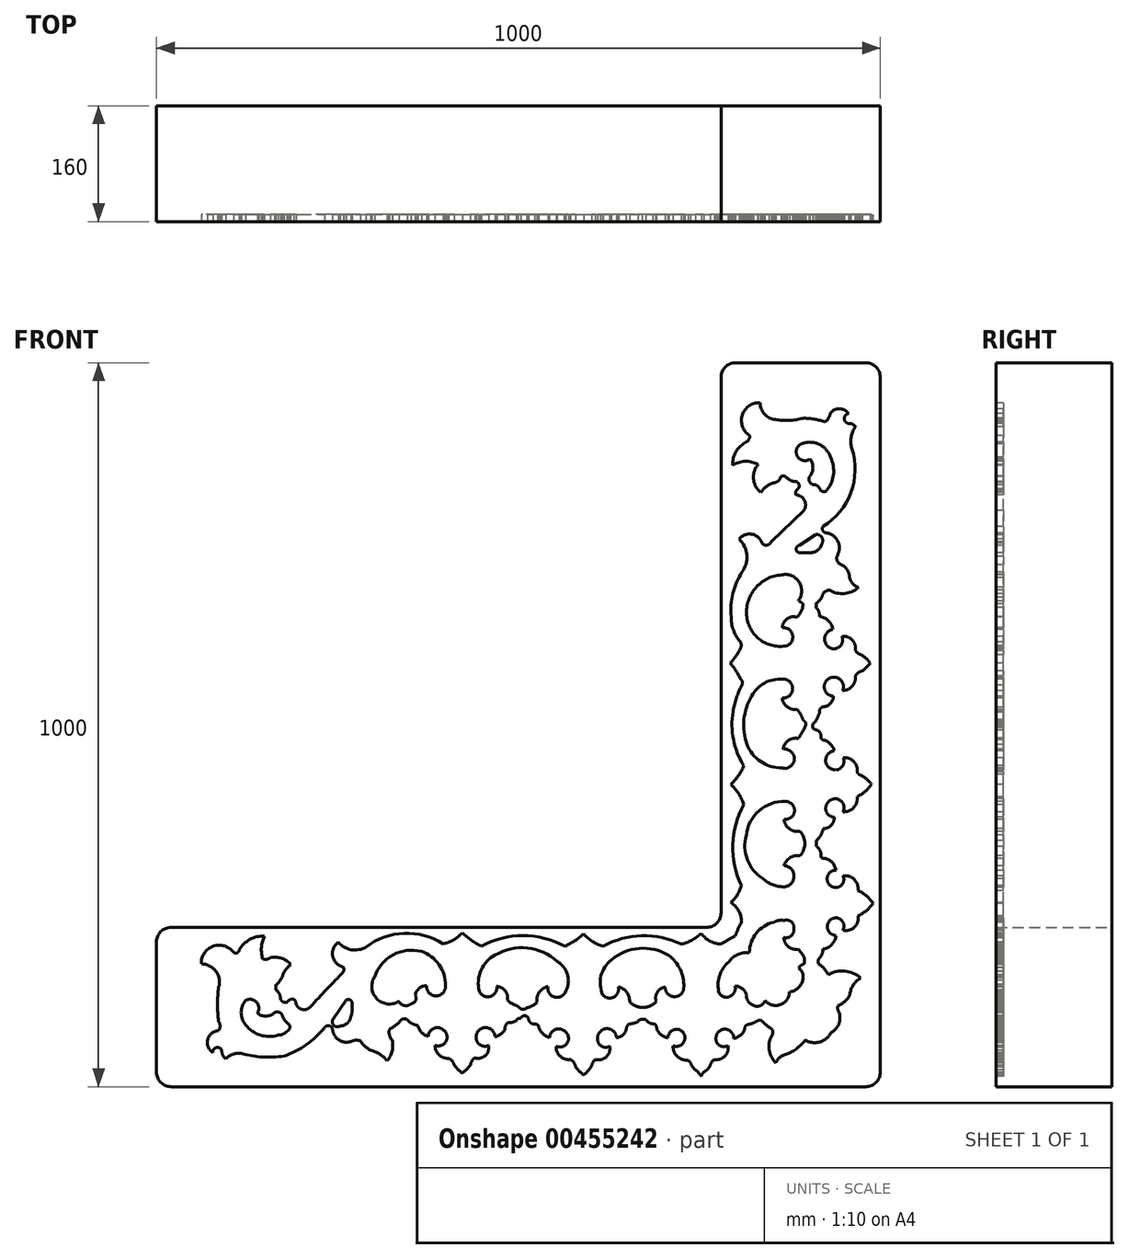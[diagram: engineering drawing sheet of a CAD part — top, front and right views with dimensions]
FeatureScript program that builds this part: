
annotation { "Feature Type Name" : "Feature", "Feature Type Description" : "" }
export const myFeature = defineFeature(function(context is Context, id is Id, definition is map)
    precondition{}
    {
        {
            var Q0;
            Q0=qCreatedBy(makeId("Front.planeOp"),FACE);
            var sketch = newSketch(context, id + "F0", { "sketchPlane" : qUnion([Q0])});
            skLineSegment(sketch, "E0", {"start": v(293.54, 525.11) * mm, "end": v(513.54, 525.11) * mm});
            skLineSegment(sketch, "E1", {"start": v(513.54, 525.11) * mm, "end": v(513.54, -474.89) * mm});
            skLineSegment(sketch, "E2", {"start": v(513.54, -474.89) * mm, "end": v(-486.46, -474.89) * mm});
            skLineSegment(sketch, "E3", {"start": v(-486.46, -474.89) * mm, "end": v(-486.46, -254.89) * mm});
            skLineSegment(sketch, "E4", {"start": v(-486.46, -254.89) * mm, "end": v(293.54, -254.89) * mm});
            skLineSegment(sketch, "E5", {"start": v(293.54, -254.89) * mm, "end": v(293.54, 525.11) * mm});
            skSolve(sketch);
        }
        {
            var Q0;
            Q0=makeQuery(id+"F0.imprint","IMPRINT",FACE,{"disambiguationData":[TD([[makeQuery(id+"F0.imprint","IMPRINT",EDGE,{"derivedFrom":sQuery(id+"F0.wireOp",EDGE,"E0")}),-1.0]])]});
            extrude(context, id + "F1", {"entities" : qUnion([Q0]), "depth" : 160 * mm, "offsetDistance" : 25 * mm});
        }
        {
            var Q0;
            Q0=makeQuery(id+"F1.opExtrude","CAP_FACE",FACE,{"disambiguationData":[OSD([sQuery(id+"F0.wireOp",EDGE,"E0"),sQuery(id+"F0.wireOp",EDGE,"E1"),sQuery(id+"F0.wireOp",EDGE,"E2"),sQuery(id+"F0.wireOp",EDGE,"E3"),sQuery(id+"F0.wireOp",EDGE,"E4"),sQuery(id+"F0.wireOp",EDGE,"E5")])],"isStart":false});
            var sketch = newSketch(context, id + "F2", { "sketchPlane" : qUnion([Q0])});
            skLineSegment(sketch, "E6.0", {"start": v(-486.46, -474.89) * mm, "end": v(-486.46, -254.89) * mm});
            skLineSegment(sketch, "E7.0", {"start": v(-486.46, -254.89) * mm, "end": v(293.54, -254.89) * mm});
            skLineSegment(sketch, "E8.0", {"start": v(293.54, -254.89) * mm, "end": v(293.54, 525.11) * mm});
            skLineSegment(sketch, "E9.0", {"start": v(513.54, 525.11) * mm, "end": v(513.54, -474.89) * mm});
            skLineSegment(sketch, "E10.0", {"start": v(293.54, 525.11) * mm, "end": v(513.54, 525.11) * mm});
            skLineSegment(sketch, "E11.0", {"start": v(513.54, -474.89) * mm, "end": v(-486.46, -474.89) * mm});
            skPoint(sketch, "E12", {"position": v(347.58, 469.9) * mm});
            skPoint(sketch, "E13", {"position": v(469.47, 454.84) * mm});
            skPoint(sketch, "E14", {"position": v(479.4, 436.57) * mm});
            skPoint(sketch, "E15", {"position": v(416.47, 392.08) * mm});
            skPoint(sketch, "E16", {"position": v(309.46, 383.32) * mm});
            skPoint(sketch, "E17", {"position": v(348.57, 346) * mm});
            skPoint(sketch, "E18", {"position": v(397.01, 342.64) * mm});
            skArc(sketch, "E19", {"start": v(347.58, 469.9) * mm, "mid": v(322.83, 452.99) * mm, "end": v(333.09, 424.82) * mm});
            skArc(sketch, "E20", {"start": v(347.58, 469.9) * mm, "mid": v(353.59, 454.2) * mm, "end": v(368.62, 446.67) * mm});
            skArc(sketch, "E21", {"start": v(368.62, 446.67) * mm, "mid": v(387.58, 445.56) * mm, "end": v(406.34, 448.47) * mm});
            skArc(sketch, "E22", {"start": v(436.71, 443.51) * mm, "mid": v(421.76, 447.44) * mm, "end": v(406.34, 448.47) * mm});
            skArc(sketch, "E23", {"start": v(436.71, 443.51) * mm, "mid": v(441.95, 448.43) * mm, "end": v(444.26, 455.23) * mm});
            skArc(sketch, "E24", {"start": v(469.47, 454.84) * mm, "mid": v(456.97, 461.6) * mm, "end": v(444.26, 455.23) * mm});
            skArc(sketch, "E25", {"start": v(469.47, 454.84) * mm, "mid": v(463.74, 448.09) * mm, "end": v(469.47, 441.34) * mm});
            skArc(sketch, "E26", {"start": v(479.4, 436.57) * mm, "mid": v(475.12, 440.38) * mm, "end": v(469.47, 441.34) * mm});
            skArc(sketch, "E27", {"start": v(328.32, 415.69) * mm, "mid": v(332.21, 419.47) * mm, "end": v(333.09, 424.82) * mm});
            skArc(sketch, "E28", {"start": v(328.32, 415.69) * mm, "mid": v(314.23, 402.22) * mm, "end": v(309.46, 383.32) * mm});
            skArc(sketch, "E29", {"start": v(344.66, 384.5) * mm, "mid": v(326.9, 389.02) * mm, "end": v(309.46, 383.32) * mm});
            skArc(sketch, "E30", {"start": v(344.66, 384.5) * mm, "mid": v(338.42, 364.41) * mm, "end": v(348.57, 346) * mm});
            skArc(sketch, "E31", {"start": v(368.62, 359.7) * mm, "mid": v(357.18, 354.93) * mm, "end": v(348.57, 346) * mm});
            skArc(sketch, "E32", {"start": v(368.62, 359.7) * mm, "mid": v(373.45, 362.8) * mm, "end": v(376.17, 367.85) * mm});
            skArc(sketch, "E33", {"start": v(382.92, 367.85) * mm, "mid": v(379.54, 368.86) * mm, "end": v(376.17, 367.85) * mm});
            skArc(sketch, "E34", {"start": v(405.15, 413.52) * mm, "mid": v(398.78, 396.46) * mm, "end": v(416.47, 392.08) * mm});
            skArc(sketch, "E35", {"start": v(444.65, 394.87) * mm, "mid": v(428.84, 412.53) * mm, "end": v(405.15, 413.52) * mm});
            skArc(sketch, "E36", {"start": v(416.47, 368.86) * mm, "mid": v(420.54, 380.47) * mm, "end": v(416.47, 392.08) * mm});
            skPoint(sketch, "E36.startSnap0", {"position": v(379.54, 368.86) * mm});
            skArc(sketch, "E37", {"start": v(416.47, 368.86) * mm, "mid": v(416.06, 360.33) * mm, "end": v(423.81, 356.74) * mm});
            skArc(sketch, "E38", {"start": v(431.55, 348.6) * mm, "mid": v(428.43, 353.38) * mm, "end": v(423.81, 356.74) * mm});
            skArc(sketch, "E39", {"start": v(438.7, 347.61) * mm, "mid": v(448.83, 370.34) * mm, "end": v(444.65, 394.87) * mm});
            skArc(sketch, "E40", {"start": v(431.55, 348.6) * mm, "mid": v(435, 347.14) * mm, "end": v(438.7, 347.61) * mm});
            skArc(sketch, "E41", {"start": v(382.92, 367.85) * mm, "mid": v(389.55, 362.82) * mm, "end": v(397.65, 360.91) * mm});
            skArc(sketch, "E42", {"start": v(479.4, 436.57) * mm, "mid": v(473.26, 422.25) * mm, "end": v(474.29, 406.7) * mm});
            skArc(sketch, "E43", {"start": v(434.42, 298.87) * mm, "mid": v(472.97, 345.9) * mm, "end": v(474.29, 406.7) * mm});
            skArc(sketch, "E44", {"start": v(434.42, 298.87) * mm, "mid": v(434.35, 293) * mm, "end": v(439.48, 290.16) * mm});
            skArc(sketch, "E45", {"start": v(400.17, 351.09) * mm, "mid": v(401.39, 356.64) * mm, "end": v(397.65, 360.91) * mm});
            skArc(sketch, "E46", {"start": v(400.17, 351.09) * mm, "mid": v(396.92, 347.49) * mm, "end": v(397.01, 342.64) * mm});
            skArc(sketch, "E47", {"start": v(408.31, 321.32) * mm, "mid": v(408.75, 335.21) * mm, "end": v(397.01, 342.64) * mm});
            skLineSegment(sketch, "E48", {"start": v(408.31, 321.32) * mm, "end": v(362.74, 277.98) * mm});
            skArc(sketch, "E49", {"start": v(350, 276.2) * mm, "mid": v(356.91, 273.14) * mm, "end": v(362.74, 277.98) * mm});
            skArc(sketch, "E50", {"start": v(350, 276.2) * mm, "mid": v(335.85, 288.38) * mm, "end": v(318.5, 281.52) * mm});
            skArc(sketch, "E51", {"start": v(433.32, 276.2) * mm, "mid": v(432.24, 284.82) * mm, "end": v(424.05, 287.72) * mm});
            skArc(sketch, "E52", {"start": v(415.91, 262.73) * mm, "mid": v(427.12, 266.23) * mm, "end": v(433.32, 276.2) * mm});
            skLineSegment(sketch, "E53", {"start": v(424.05, 287.72) * mm, "end": v(401.6, 272.84) * mm});
            skLineSegment(sketch, "E54", {"start": v(415.91, 262.73) * mm, "end": v(402.44, 262.73) * mm});
            skArc(sketch, "E55", {"start": v(401.6, 272.84) * mm, "mid": v(397.36, 267.4) * mm, "end": v(402.44, 262.73) * mm});
            skArc(sketch, "E56", {"start": v(453.53, 257.97) * mm, "mid": v(455.25, 277.88) * mm, "end": v(439.48, 290.16) * mm});
            skArc(sketch, "E57", {"start": v(453.53, 257.97) * mm, "mid": v(454.5, 250.96) * mm, "end": v(459.7, 246.17) * mm});
            skArc(sketch, "E58", {"start": v(322.42, 235.75) * mm, "mid": v(329.22, 259.39) * mm, "end": v(318.5, 281.52) * mm});
            skArc(sketch, "E59", {"start": v(322.42, 235.75) * mm, "mid": v(309.83, 206.4) * mm, "end": v(307.54, 174.54) * mm});
            skArc(sketch, "E60", {"start": v(471.16, 228.58) * mm, "mid": v(467.9, 238.98) * mm, "end": v(459.7, 246.17) * mm});
            skArc(sketch, "E61", {"start": v(471.16, 228.58) * mm, "mid": v(475.53, 220.14) * mm, "end": v(483.44, 214.88) * mm});
            skArc(sketch, "E62", {"start": v(443.28, 211.3) * mm, "mid": v(463.96, 206.3) * mm, "end": v(483.44, 214.88) * mm});
            skArc(sketch, "E63", {"start": v(443.28, 211.3) * mm, "mid": v(436.25, 208.03) * mm, "end": v(432.89, 201.05) * mm});
            skArc(sketch, "E64", {"start": v(424.75, 192.2) * mm, "mid": v(429.03, 196.42) * mm, "end": v(432.89, 201.05) * mm});
            skArc(sketch, "E65", {"start": v(398.3, 173.7) * mm, "mid": v(384.6, 171.37) * mm, "end": v(378.1, 159.1) * mm});
            skArc(sketch, "E66", {"start": v(398.3, 173.7) * mm, "mid": v(404.56, 181.95) * mm, "end": v(406.87, 192.04) * mm});
            skArc(sketch, "E67", {"start": v(406.87, 192.04) * mm, "mid": v(403.8, 194.52) * mm, "end": v(400.27, 196.25) * mm});
            skArc(sketch, "E68", {"start": v(400.27, 196.25) * mm, "mid": v(401.46, 222.16) * mm, "end": v(377.52, 232.15) * mm});
            skArc(sketch, "E69", {"start": v(377.52, 232.15) * mm, "mid": v(340.66, 213.44) * mm, "end": v(329.28, 173.7) * mm});
            skArc(sketch, "E70", {"start": v(329.28, 173.7) * mm, "mid": v(348.5, 141.77) * mm, "end": v(385.06, 134.46) * mm});
            skArc(sketch, "E71", {"start": v(385.06, 134.46) * mm, "mid": v(392.23, 149.8) * mm, "end": v(378.1, 159.1) * mm});
            skArc(sketch, "E72", {"start": v(424.75, 187.29) * mm, "mid": v(425, 189.74) * mm, "end": v(424.75, 192.2) * mm});
            skArc(sketch, "E73", {"start": v(429.85, 174.76) * mm, "mid": v(428.5, 181.51) * mm, "end": v(424.75, 187.29) * mm});
            skArc(sketch, "E74", {"start": v(447.96, 156.74) * mm, "mid": v(441.92, 168.78) * mm, "end": v(429.85, 174.76) * mm});
            skArc(sketch, "E75", {"start": v(447.96, 156.74) * mm, "mid": v(436.73, 144.75) * mm, "end": v(445.2, 130.69) * mm});
            skArc(sketch, "E76", {"start": v(445.2, 130.69) * mm, "mid": v(458.3, 133.93) * mm, "end": v(460.73, 147.22) * mm});
            skArc(sketch, "E77", {"start": v(479.17, 127.6) * mm, "mid": v(474.95, 142.12) * mm, "end": v(460.73, 147.22) * mm});
            skArc(sketch, "E78", {"start": v(479.17, 127.6) * mm, "mid": v(482.66, 123.94) * mm, "end": v(487.27, 121.85) * mm});
            skArc(sketch, "E79", {"start": v(499.62, 110.08) * mm, "mid": v(494.12, 116.68) * mm, "end": v(487.27, 121.85) * mm});
            skArc(sketch, "E80", {"start": v(489.02, 99.56) * mm, "mid": v(494.55, 104.59) * mm, "end": v(499.62, 110.08) * mm});
            skArc(sketch, "E81", {"start": v(489.02, 99.56) * mm, "mid": v(483.3, 97.11) * mm, "end": v(479.17, 92.46) * mm});
            skArc(sketch, "E82", {"start": v(461.64, 72.5) * mm, "mid": v(474.9, 78.54) * mm, "end": v(479.17, 92.46) * mm});
            skArc(sketch, "E83", {"start": v(461.64, 72.5) * mm, "mid": v(457.56, 88.1) * mm, "end": v(441.44, 88.11) * mm});
            skArc(sketch, "E84", {"start": v(441.44, 88.11) * mm, "mid": v(436.73, 73.71) * mm, "end": v(448.87, 64.66) * mm});
            skArc(sketch, "E85", {"start": v(433.43, 49.63) * mm, "mid": v(444.2, 54) * mm, "end": v(448.87, 64.66) * mm});
            skArc(sketch, "E86", {"start": v(307.54, 174.54) * mm, "mid": v(310.68, 155.8) * mm, "end": v(320.4, 139.47) * mm});
            skArc(sketch, "E87", {"start": v(320.4, 130.69) * mm, "mid": v(321.5, 135.08) * mm, "end": v(320.4, 139.47) * mm});
            skArc(sketch, "E88", {"start": v(306, 110.08) * mm, "mid": v(313.99, 119.83) * mm, "end": v(320.4, 130.69) * mm});
            skArc(sketch, "E89", {"start": v(320.4, 88.11) * mm, "mid": v(314.12, 99.7) * mm, "end": v(306, 110.08) * mm});
            skArc(sketch, "E90", {"start": v(322.16, 79.73) * mm, "mid": v(323.1, 84.3) * mm, "end": v(320.4, 88.11) * mm});
            skArc(sketch, "E91", {"start": v(322.16, 79.73) * mm, "mid": v(314.8, 62.04) * mm, "end": v(310.05, 43.47) * mm});
            skArc(sketch, "E92", {"start": v(378.1, 62.07) * mm, "mid": v(392.48, 75.09) * mm, "end": v(378.1, 88.11) * mm});
            skArc(sketch, "E93", {"start": v(378.1, 88.11) * mm, "mid": v(353.53, 82.59) * mm, "end": v(335.85, 64.66) * mm});
            skArc(sketch, "E94", {"start": v(335.85, 64.66) * mm, "mid": v(325.2, 32.09) * mm, "end": v(329.28, -1.93) * mm});
            skArc(sketch, "E95", {"start": v(329.28, -1.93) * mm, "mid": v(348.37, -25.67) * mm, "end": v(377.52, -34.5) * mm});
            skArc(sketch, "E96", {"start": v(377.52, -34.5) * mm, "mid": v(394.75, -22.84) * mm, "end": v(379.39, -8.8) * mm});
            skArc(sketch, "E97", {"start": v(400.27, 6.1) * mm, "mid": v(386.48, 3.34) * mm, "end": v(379.39, -8.8) * mm});
            skArc(sketch, "E98", {"start": v(400.27, 6.1) * mm, "mid": v(405.46, 14.63) * mm, "end": v(410.26, 23.38) * mm});
            skArc(sketch, "E99", {"start": v(410.26, 23.38) * mm, "mid": v(410.47, 25.96) * mm, "end": v(410.26, 28.54) * mm});
            skArc(sketch, "E100", {"start": v(406.87, 32.11) * mm, "mid": v(408.47, 30.24) * mm, "end": v(410.26, 28.54) * mm});
            skArc(sketch, "E101", {"start": v(406.87, 32.11) * mm, "mid": v(403.36, 39.64) * mm, "end": v(398.55, 46.4) * mm});
            skArc(sketch, "E102", {"start": v(378.1, 62.07) * mm, "mid": v(384.92, 49.8) * mm, "end": v(398.55, 46.4) * mm});
            skArc(sketch, "E103", {"start": v(433.43, 49.63) * mm, "mid": v(430.18, 46.57) * mm, "end": v(429.76, 42.13) * mm});
            skArc(sketch, "E104", {"start": v(424.3, 30.21) * mm, "mid": v(427.3, 36.05) * mm, "end": v(429.76, 42.13) * mm});
            skArc(sketch, "E105", {"start": v(420.18, 25.8) * mm, "mid": v(422.36, 27.9) * mm, "end": v(424.3, 30.21) * mm});
            skArc(sketch, "E106", {"start": v(420.18, 25.8) * mm, "mid": v(420.18, 23.34) * mm, "end": v(420.18, 20.88) * mm});
            skArc(sketch, "E107", {"start": v(420.18, 20.88) * mm, "mid": v(423.46, 18.46) * mm, "end": v(427.43, 17.56) * mm});
            skArc(sketch, "E108", {"start": v(431.7, 6.49) * mm, "mid": v(431.15, 12.63) * mm, "end": v(427.43, 17.56) * mm});
            skArc(sketch, "E109", {"start": v(431.7, 6.49) * mm, "mid": v(432.9, 5.2) * mm, "end": v(434.33, 4.15) * mm});
            skArc(sketch, "E110", {"start": v(450.05, -10.93) * mm, "mid": v(444.35, -1.14) * mm, "end": v(434.33, 4.15) * mm});
            skArc(sketch, "E111", {"start": v(450.05, -10.93) * mm, "mid": v(438.12, -22.73) * mm, "end": v(447.63, -36.56) * mm});
            skArc(sketch, "E112", {"start": v(447.63, -36.56) * mm, "mid": v(460.43, -33.49) * mm, "end": v(462.15, -20.44) * mm});
            skArc(sketch, "E113", {"start": v(481.53, -40.4) * mm, "mid": v(476.91, -25.5) * mm, "end": v(462.15, -20.44) * mm});
            skArc(sketch, "E114", {"start": v(481.53, -40.4) * mm, "mid": v(482.7, -41.95) * mm, "end": v(483.91, -43.48) * mm});
            skArc(sketch, "E115", {"start": v(501.38, -57.47) * mm, "mid": v(493.74, -49.1) * mm, "end": v(483.91, -43.48) * mm});
            skArc(sketch, "E116", {"start": v(481.53, -74.25) * mm, "mid": v(492.52, -67.12) * mm, "end": v(501.38, -57.47) * mm});
            skArc(sketch, "E117", {"start": v(462.15, -95.1) * mm, "mid": v(476.86, -89.34) * mm, "end": v(481.53, -74.25) * mm});
            skArc(sketch, "E118", {"start": v(462.15, -95.1) * mm, "mid": v(458.24, -79.38) * mm, "end": v(442.12, -81.11) * mm});
            skArc(sketch, "E119", {"start": v(442.12, -81.11) * mm, "mid": v(438.9, -94.5) * mm, "end": v(450.05, -102.55) * mm});
            skArc(sketch, "E120", {"start": v(310.05, 43.47) * mm, "mid": v(310.73, 4.66) * mm, "end": v(325.01, -31.44) * mm});
            skArc(sketch, "E121", {"start": v(306.98, -57.47) * mm, "mid": v(317.39, -45.42) * mm, "end": v(325.01, -31.44) * mm});
            skArc(sketch, "E122", {"start": v(325.01, -85.2) * mm, "mid": v(317.82, -70.15) * mm, "end": v(306.98, -57.47) * mm});
            skArc(sketch, "E123", {"start": v(434.84, -118.46) * mm, "mid": v(445.75, -113.67) * mm, "end": v(450.05, -102.55) * mm});
            skArc(sketch, "E124", {"start": v(425.7, -134.54) * mm, "mid": v(431.5, -127.19) * mm, "end": v(434.84, -118.46) * mm});
            skArc(sketch, "E125", {"start": v(425.7, -134.54) * mm, "mid": v(424.98, -138.9) * mm, "end": v(425.7, -143.28) * mm});
            skArc(sketch, "E126", {"start": v(380.49, -105.27) * mm, "mid": v(395.08, -94.2) * mm, "end": v(382.49, -80.9) * mm});
            skArc(sketch, "E127", {"start": v(382.49, -80.9) * mm, "mid": v(346.23, -93.37) * mm, "end": v(328.4, -127.33) * mm});
            skArc(sketch, "E128", {"start": v(328.4, -127.33) * mm, "mid": v(330.01, -161.32) * mm, "end": v(351.44, -187.76) * mm});
            skArc(sketch, "E129", {"start": v(380.49, -105.27) * mm, "mid": v(387.75, -118.57) * mm, "end": v(402.52, -121.96) * mm});
            skArc(sketch, "E130", {"start": v(402.52, -156.03) * mm, "mid": v(409.2, -139) * mm, "end": v(402.52, -121.96) * mm});
            skArc(sketch, "E131", {"start": v(402.52, -156.03) * mm, "mid": v(388.96, -158.51) * mm, "end": v(380.49, -169.39) * mm});
            skArc(sketch, "E132", {"start": v(380.49, -198.77) * mm, "mid": v(394.42, -184.08) * mm, "end": v(380.49, -169.39) * mm});
            skArc(sketch, "E133", {"start": v(351.44, -187.76) * mm, "mid": v(364.98, -195.87) * mm, "end": v(380.49, -198.77) * mm});
            skArc(sketch, "E134", {"start": v(325.01, -85.2) * mm, "mid": v(309.9, -140.73) * mm, "end": v(321.7, -197.04) * mm});
            skArc(sketch, "E135", {"start": v(307.17, -220.71) * mm, "mid": v(316.08, -209.89) * mm, "end": v(321.7, -197.04) * mm});
            skArc(sketch, "E136", {"start": v(321.7, -247.76) * mm, "mid": v(318.08, -232.28) * mm, "end": v(307.17, -220.71) * mm});
            skArc(sketch, "E137", {"start": v(431.66, -156.32) * mm, "mid": v(430.48, -148.98) * mm, "end": v(425.7, -143.28) * mm});
            skArc(sketch, "E138", {"start": v(431.66, -156.32) * mm, "mid": v(432.35, -158.42) * mm, "end": v(434.4, -159.24) * mm});
            skArc(sketch, "E139", {"start": v(452.27, -175.77) * mm, "mid": v(446.32, -164.28) * mm, "end": v(434.4, -159.24) * mm});
            skArc(sketch, "E140", {"start": v(452.27, -175.77) * mm, "mid": v(440.25, -185.87) * mm, "end": v(448.52, -199.23) * mm});
            skArc(sketch, "E141", {"start": v(448.52, -199.23) * mm, "mid": v(460.47, -196) * mm, "end": v(461.87, -183.7) * mm});
            skArc(sketch, "E142", {"start": v(482.66, -203.73) * mm, "mid": v(477.43, -188.35) * mm, "end": v(461.87, -183.7) * mm});
            skArc(sketch, "E143", {"start": v(503.48, -221.46) * mm, "mid": v(494.23, -211.24) * mm, "end": v(482.66, -203.73) * mm});
            skArc(sketch, "E144", {"start": v(482.66, -238.94) * mm, "mid": v(494.27, -231.63) * mm, "end": v(503.48, -221.46) * mm});
            skArc(sketch, "E145", {"start": v(461.87, -258.6) * mm, "mid": v(477.81, -254.63) * mm, "end": v(482.66, -238.94) * mm});
            skArc(sketch, "E146", {"start": v(461.87, -258.6) * mm, "mid": v(459.78, -244.64) * mm, "end": v(445.71, -243.61) * mm});
            skArc(sketch, "E147", {"start": v(445.71, -243.61) * mm, "mid": v(441.02, -257.16) * mm, "end": v(452.27, -266.05) * mm});
            skArc(sketch, "E148", {"start": v(434.4, -284.89) * mm, "mid": v(446.58, -278.54) * mm, "end": v(452.27, -266.05) * mm});
            skArc(sketch, "E149", {"start": v(427.74, -299.41) * mm, "mid": v(432.54, -292.82) * mm, "end": v(434.4, -284.89) * mm});
            skArc(sketch, "E150", {"start": v(427.74, -304.96) * mm, "mid": v(427.94, -302.19) * mm, "end": v(427.74, -299.41) * mm});
            skArc(sketch, "E151", {"start": v(441.45, -320.38) * mm, "mid": v(435.83, -311.57) * mm, "end": v(427.74, -304.96) * mm});
            skArc(sketch, "E152", {"start": v(486.54, -324.86) * mm, "mid": v(464.73, -315.23) * mm, "end": v(441.45, -320.38) * mm});
            skArc(sketch, "E153", {"start": v(486.54, -324.86) * mm, "mid": v(476.22, -334.3) * mm, "end": v(471.67, -347.53) * mm});
            skArc(sketch, "E154", {"start": v(455.38, -362.88) * mm, "mid": v(465, -356.77) * mm, "end": v(471.67, -347.53) * mm});
            skArc(sketch, "E155", {"start": v(455.38, -362.88) * mm, "mid": v(454.62, -366.12) * mm, "end": v(455.38, -369.36) * mm});
            skArc(sketch, "E156", {"start": v(445.71, -399.91) * mm, "mid": v(456.89, -386.64) * mm, "end": v(455.38, -369.36) * mm});
            skArc(sketch, "E157", {"start": v(409.82, -410.44) * mm, "mid": v(430.07, -413.03) * mm, "end": v(445.71, -399.91) * mm});
            skArc(sketch, "E158", {"start": v(381.1, -430.98) * mm, "mid": v(397, -422.86) * mm, "end": v(409.82, -410.44) * mm});
            skArc(sketch, "E159", {"start": v(381.1, -430.98) * mm, "mid": v(373.79, -435.06) * mm, "end": v(369.09, -442) * mm});
            skArc(sketch, "E160", {"start": v(380.18, -268.77) * mm, "mid": v(386.7, -281.45) * mm, "end": v(400.53, -284.89) * mm});
            skArc(sketch, "E161", {"start": v(408.37, -296.17) * mm, "mid": v(404.64, -290.4) * mm, "end": v(400.53, -284.89) * mm});
            skArc(sketch, "E162", {"start": v(408.37, -304.96) * mm, "mid": v(408.93, -300.56) * mm, "end": v(408.37, -296.17) * mm});
            skArc(sketch, "E163", {"start": v(408.37, -304.96) * mm, "mid": v(404, -307.26) * mm, "end": v(400.53, -310.78) * mm});
            skArc(sketch, "E164", {"start": v(406.35, -327.76) * mm, "mid": v(406.36, -318.27) * mm, "end": v(400.53, -310.78) * mm});
            skArc(sketch, "E165", {"start": v(388.18, -343.88) * mm, "mid": v(399.85, -338.74) * mm, "end": v(406.35, -327.76) * mm});
            skArc(sketch, "E166", {"start": v(354.3, -355.75) * mm, "mid": v(375.38, -361.62) * mm, "end": v(388.18, -343.88) * mm});
            skArc(sketch, "E167", {"start": v(337.3, -362.01) * mm, "mid": v(347.37, -363.14) * mm, "end": v(354.3, -355.75) * mm});
            skArc(sketch, "E168", {"start": v(328.45, -347.53) * mm, "mid": v(330.46, -356.25) * mm, "end": v(337.3, -362.01) * mm});
            skArc(sketch, "E169", {"start": v(328.45, -347.53) * mm, "mid": v(322.61, -339.1) * mm, "end": v(312.87, -335.93) * mm});
            skArc(sketch, "E170", {"start": v(291.01, -346.06) * mm, "mid": v(306.16, -350.11) * mm, "end": v(312.87, -335.93) * mm});
            skArc(sketch, "E171", {"start": v(304.41, -302.19) * mm, "mid": v(291.34, -322.18) * mm, "end": v(291.01, -346.06) * mm});
            skArc(sketch, "E172", {"start": v(332.8, -289.76) * mm, "mid": v(316.93, -292.15) * mm, "end": v(304.41, -302.19) * mm});
            skArc(sketch, "E173", {"start": v(366.55, -247.76) * mm, "mid": v(342.32, -262.85) * mm, "end": v(332.8, -289.76) * mm});
            skArc(sketch, "E174", {"start": v(380.18, -268.77) * mm, "mid": v(390.48, -266.4) * mm, "end": v(394.14, -256.48) * mm});
            skArc(sketch, "E175", {"start": v(394.14, -256.48) * mm, "mid": v(390.8, -247.14) * mm, "end": v(381.04, -245.27) * mm});
            skArc(sketch, "E176", {"start": v(381.04, -245.27) * mm, "mid": v(373.56, -245.17) * mm, "end": v(366.55, -247.76) * mm});
            skArc(sketch, "E177", {"start": v(364.8, -402.2) * mm, "mid": v(359.96, -422.85) * mm, "end": v(369.09, -442) * mm});
            skArc(sketch, "E178", {"start": v(364.8, -402.2) * mm, "mid": v(365.17, -399.16) * mm, "end": v(364.8, -396.12) * mm});
            skArc(sketch, "E179", {"start": v(349.7, -383.55) * mm, "mid": v(356.82, -390.36) * mm, "end": v(364.8, -396.12) * mm});
            skArc(sketch, "E180", {"start": v(349.7, -383.55) * mm, "mid": v(346.95, -383.31) * mm, "end": v(344.2, -383.55) * mm});
            skArc(sketch, "E181", {"start": v(330.75, -388.92) * mm, "mid": v(337.8, -387.05) * mm, "end": v(344.2, -383.55) * mm});
            skArc(sketch, "E182", {"start": v(330.75, -388.92) * mm, "mid": v(327.04, -391.66) * mm, "end": v(326.17, -396.18) * mm});
            skArc(sketch, "E183", {"start": v(310.98, -408.2) * mm, "mid": v(320.1, -404.13) * mm, "end": v(326.17, -396.18) * mm});
            skArc(sketch, "E184", {"start": v(310.98, -408.2) * mm, "mid": v(299.84, -395.38) * mm, "end": v(286.69, -406.13) * mm});
            skArc(sketch, "E185", {"start": v(286.69, -406.13) * mm, "mid": v(290.96, -417.53) * mm, "end": v(303.13, -417.98) * mm});
            skArc(sketch, "E186", {"start": v(284.35, -437.24) * mm, "mid": v(298.93, -432.66) * mm, "end": v(303.13, -417.98) * mm});
            skArc(sketch, "E187", {"start": v(284.35, -437.24) * mm, "mid": v(280.52, -440.94) * mm, "end": v(278.52, -445.87) * mm});
            skArc(sketch, "E188", {"start": v(269.75, -454.8) * mm, "mid": v(274.72, -450.9) * mm, "end": v(278.52, -445.87) * mm});
            skArc(sketch, "E189", {"start": v(269.75, -454.8) * mm, "mid": v(267.43, -457.44) * mm, "end": v(266.24, -460.76) * mm});
            skArc(sketch, "E190", {"start": v(251.29, -441.32) * mm, "mid": v(254.05, -447.1) * mm, "end": v(258.45, -451.77) * mm});
            skArc(sketch, "E191", {"start": v(266.24, -460.76) * mm, "mid": v(262.73, -455.93) * mm, "end": v(258.45, -451.77) * mm});
            skArc(sketch, "E192", {"start": v(247.97, -438.2) * mm, "mid": v(249.62, -439.77) * mm, "end": v(251.29, -441.32) * mm});
            skArc(sketch, "E193", {"start": v(227.21, -418.36) * mm, "mid": v(233.11, -432.97) * mm, "end": v(247.97, -438.2) * mm});
            skArc(sketch, "E194", {"start": v(227.21, -418.36) * mm, "mid": v(241.14, -414.61) * mm, "end": v(241.4, -400.2) * mm});
            skArc(sketch, "E195", {"start": v(241.4, -400.2) * mm, "mid": v(228.24, -396.16) * mm, "end": v(220.28, -407.4) * mm});
            skArc(sketch, "E196", {"start": v(321.7, -247.76) * mm, "mid": v(316.93, -257.23) * mm, "end": v(312.98, -267.07) * mm});
            skArc(sketch, "E197", {"start": v(312.98, -267.07) * mm, "mid": v(303.04, -272.23) * mm, "end": v(293.33, -277.8) * mm});
            skArc(sketch, "E198", {"start": v(266.24, -262.92) * mm, "mid": v(277.93, -273.73) * mm, "end": v(293.33, -277.8) * mm});
            skArc(sketch, "E199", {"start": v(238.34, -277.8) * mm, "mid": v(253.35, -272.35) * mm, "end": v(266.24, -262.92) * mm});
            skArc(sketch, "E200", {"start": v(203.97, -391.07) * mm, "mid": v(209.35, -402) * mm, "end": v(220.28, -407.4) * mm});
            skArc(sketch, "E201", {"start": v(238.34, -277.8) * mm, "mid": v(184.16, -266.27) * mm, "end": v(130.71, -280.82) * mm});
            skArc(sketch, "E202", {"start": v(203.97, -391.07) * mm, "mid": v(202.2, -388.55) * mm, "end": v(199.17, -388.02) * mm});
            skArc(sketch, "E203", {"start": v(189.49, -382.1) * mm, "mid": v(193.64, -386.18) * mm, "end": v(199.17, -388.02) * mm});
            skArc(sketch, "E204", {"start": v(189.49, -382.1) * mm, "mid": v(186.98, -381.8) * mm, "end": v(184.48, -382.1) * mm});
            skArc(sketch, "E205", {"start": v(184.48, -382.1) * mm, "mid": v(181.07, -382.53) * mm, "end": v(178.7, -385) * mm});
            skArc(sketch, "E206", {"start": v(167.14, -388.02) * mm, "mid": v(173.08, -387.14) * mm, "end": v(178.7, -385) * mm});
            skArc(sketch, "E207", {"start": v(167.14, -388.02) * mm, "mid": v(163.67, -391.5) * mm, "end": v(162.6, -396.29) * mm});
            skArc(sketch, "E208", {"start": v(167.14, -357.28) * mm, "mid": v(163.15, -344.26) * mm, "end": v(151.55, -337.13) * mm});
            skArc(sketch, "E209", {"start": v(167.14, -357.28) * mm, "mid": v(185.55, -365.32) * mm, "end": v(203.97, -357.28) * mm});
            skArc(sketch, "E210", {"start": v(216.4, -337.29) * mm, "mid": v(205.45, -344.34) * mm, "end": v(203.97, -357.28) * mm});
            skArc(sketch, "E211", {"start": v(216.4, -337.29) * mm, "mid": v(229.22, -350.53) * mm, "end": v(242.04, -337.29) * mm});
            skArc(sketch, "E212", {"start": v(242.04, -337.29) * mm, "mid": v(237.12, -312.73) * mm, "end": v(221.2, -293.38) * mm});
            skArc(sketch, "E213", {"start": v(221.2, -293.38) * mm, "mid": v(180.6, -283.76) * mm, "end": v(142, -299.62) * mm});
            skArc(sketch, "E214", {"start": v(130.19, -348.02) * mm, "mid": v(145.26, -351.2) * mm, "end": v(151.55, -337.13) * mm});
            skArc(sketch, "E215", {"start": v(142, -299.62) * mm, "mid": v(127.7, -321.77) * mm, "end": v(130.19, -348.02) * mm});
            skArc(sketch, "E216", {"start": v(149, -407.16) * mm, "mid": v(157.47, -403.81) * mm, "end": v(162.6, -396.29) * mm});
            skArc(sketch, "E217", {"start": v(149, -407.16) * mm, "mid": v(135, -394.64) * mm, "end": v(123.03, -409.13) * mm});
            skArc(sketch, "E218", {"start": v(123.03, -409.13) * mm, "mid": v(128.45, -418.98) * mm, "end": v(139.69, -418.95) * mm});
            skArc(sketch, "E219", {"start": v(103.65, -264) * mm, "mid": v(115.95, -274.39) * mm, "end": v(130.71, -280.82) * mm});
            skArc(sketch, "E220", {"start": v(77.77, -280.82) * mm, "mid": v(91.34, -273.37) * mm, "end": v(103.65, -264) * mm});
            skArc(sketch, "E221", {"start": v(119.98, -437.23) * mm, "mid": v(134.98, -433.64) * mm, "end": v(139.69, -418.95) * mm});
            skArc(sketch, "E222", {"start": v(119.98, -437.23) * mm, "mid": v(116.42, -441.4) * mm, "end": v(114.64, -446.58) * mm});
            skArc(sketch, "E223", {"start": v(103.65, -458.43) * mm, "mid": v(109.73, -453.06) * mm, "end": v(114.64, -446.58) * mm});
            skArc(sketch, "E224", {"start": v(92.66, -447.58) * mm, "mid": v(97.78, -453.38) * mm, "end": v(103.65, -458.43) * mm});
            skArc(sketch, "E225", {"start": v(92.66, -447.58) * mm, "mid": v(90.24, -441.63) * mm, "end": v(85.56, -437.23) * mm});
            skArc(sketch, "E226", {"start": v(65.8, -418.95) * mm, "mid": v(71.24, -432.9) * mm, "end": v(85.56, -437.23) * mm});
            skArc(sketch, "E227", {"start": v(65.8, -418.95) * mm, "mid": v(80.77, -415.02) * mm, "end": v(79.13, -399.65) * mm});
            skArc(sketch, "E228", {"start": v(79.13, -399.65) * mm, "mid": v(65.27, -395.65) * mm, "end": v(56.59, -407.16) * mm});
            skArc(sketch, "E229", {"start": v(77.77, -280.82) * mm, "mid": v(19.94, -266.18) * mm, "end": v(-37.88, -280.82) * mm});
            skArc(sketch, "E230", {"start": v(41.44, -391.57) * mm, "mid": v(46.95, -401.37) * mm, "end": v(56.59, -407.16) * mm});
            skArc(sketch, "E231", {"start": v(41.44, -391.57) * mm, "mid": v(39.24, -388.9) * mm, "end": v(35.8, -388.53) * mm});
            skArc(sketch, "E232", {"start": v(27.77, -382.68) * mm, "mid": v(30.85, -386.88) * mm, "end": v(35.8, -388.53) * mm});
            skArc(sketch, "E233", {"start": v(27.77, -382.68) * mm, "mid": v(23.08, -376.92) * mm, "end": v(16.67, -380.68) * mm});
            skArc(sketch, "E234", {"start": v(16.67, -380.68) * mm, "mid": v(13.1, -380.85) * mm, "end": v(10.85, -383.64) * mm});
            skArc(sketch, "E235", {"start": v(0, -386.05) * mm, "mid": v(5.64, -385.82) * mm, "end": v(10.85, -383.64) * mm});
            skArc(sketch, "E236", {"start": v(0, -386.05) * mm, "mid": v(-4.03, -390.08) * mm, "end": v(-4.87, -395.72) * mm});
            skArc(sketch, "E237", {"start": v(-18.8, -406.13) * mm, "mid": v(-10.78, -402.33) * mm, "end": v(-4.87, -395.72) * mm});
            skArc(sketch, "E238", {"start": v(-18.8, -406.13) * mm, "mid": v(-31.87, -393.27) * mm, "end": v(-44.93, -406.13) * mm});
            skArc(sketch, "E239", {"start": v(-44.93, -406.13) * mm, "mid": v(-39.67, -416.89) * mm, "end": v(-27.74, -417.98) * mm});
            skArc(sketch, "E240", {"start": v(-46.56, -435) * mm, "mid": v(-32.22, -431.93) * mm, "end": v(-27.74, -417.98) * mm});
            skArc(sketch, "E241", {"start": v(-46.56, -435) * mm, "mid": v(-50.77, -439.38) * mm, "end": v(-52.67, -445.17) * mm});
            skArc(sketch, "E242", {"start": v(-64.04, -455.91) * mm, "mid": v(-58.12, -450.79) * mm, "end": v(-52.67, -445.17) * mm});
            skArc(sketch, "E243", {"start": v(-75.23, -445.17) * mm, "mid": v(-69.89, -450.8) * mm, "end": v(-64.04, -455.91) * mm});
            skArc(sketch, "E244", {"start": v(-75.23, -445.17) * mm, "mid": v(-77.8, -439.5) * mm, "end": v(-82.65, -435.58) * mm});
            skArc(sketch, "E245", {"start": v(-101.6, -417.76) * mm, "mid": v(-96.14, -430.95) * mm, "end": v(-82.65, -435.58) * mm});
            skArc(sketch, "E246", {"start": v(-101.6, -417.76) * mm, "mid": v(-86.82, -412.93) * mm, "end": v(-88.8, -397.5) * mm});
            skArc(sketch, "E247", {"start": v(-88.8, -397.5) * mm, "mid": v(-102.47, -393.89) * mm, "end": v(-110.98, -405.19) * mm});
            skArc(sketch, "E248", {"start": v(-125.47, -390.25) * mm, "mid": v(-120.37, -399.8) * mm, "end": v(-110.98, -405.19) * mm});
            skArc(sketch, "E249", {"start": v(54.23, -336.61) * mm, "mid": v(61.64, -350.33) * mm, "end": v(76.86, -346.93) * mm});
            skArc(sketch, "E250", {"start": v(76.86, -346.93) * mm, "mid": v(82, -322.26) * mm, "end": v(67.22, -301.84) * mm});
            skArc(sketch, "E251", {"start": v(67.22, -301.84) * mm, "mid": v(25.88, -283.28) * mm, "end": v(-18.4, -292.87) * mm});
            skArc(sketch, "E252", {"start": v(-18.4, -292.87) * mm, "mid": v(-38.05, -314.23) * mm, "end": v(-40.45, -343.14) * mm});
            skArc(sketch, "E253", {"start": v(-40.45, -343.14) * mm, "mid": v(-25.4, -350.3) * mm, "end": v(-16.44, -336.26) * mm});
            skArc(sketch, "E254", {"start": v(-1.56, -355.2) * mm, "mid": v(-4.7, -342.36) * mm, "end": v(-16.44, -336.26) * mm});
            skArc(sketch, "E255", {"start": v(-1.56, -355.2) * mm, "mid": v(5.23, -360.43) * mm, "end": v(13.18, -363.63) * mm});
            skArc(sketch, "E256", {"start": v(54.23, -336.61) * mm, "mid": v(42.23, -344.39) * mm, "end": v(39.57, -358.43) * mm});
            skArc(sketch, "E257", {"start": v(25.1, -365.87) * mm, "mid": v(32.84, -363.13) * mm, "end": v(39.57, -358.43) * mm});
            skArc(sketch, "E258", {"start": v(13.18, -363.63) * mm, "mid": v(18.56, -367.83) * mm, "end": v(25.1, -365.87) * mm});
            skArc(sketch, "E259", {"start": v(-63.85, -262.42) * mm, "mid": v(-51.46, -272.46) * mm, "end": v(-37.88, -280.82) * mm});
            skArc(sketch, "E260", {"start": v(-90.25, -277.72) * mm, "mid": v(-75.88, -272.09) * mm, "end": v(-63.85, -262.42) * mm});
            skArc(sketch, "E261", {"start": v(-90.25, -277.72) * mm, "mid": v(-144.22, -263.01) * mm, "end": v(-196.86, -281.91) * mm});
            skArc(sketch, "E262", {"start": v(-235.17, -275.37) * mm, "mid": v(-217.2, -285.62) * mm, "end": v(-196.86, -281.91) * mm});
            skArc(sketch, "E263", {"start": v(-235.17, -275.37) * mm, "mid": v(-242.93, -294.9) * mm, "end": v(-228.03, -309.72) * mm});
            skArc(sketch, "E264", {"start": v(-139.88, -382.17) * mm, "mid": v(-133.52, -387.72) * mm, "end": v(-125.47, -390.25) * mm});
            skArc(sketch, "E265", {"start": v(-139.88, -382.17) * mm, "mid": v(-146.6, -381.6) * mm, "end": v(-151.3, -386.44) * mm});
            skArc(sketch, "E266", {"start": v(-164.7, -395.88) * mm, "mid": v(-157.84, -391.39) * mm, "end": v(-151.3, -386.44) * mm});
            skArc(sketch, "E267", {"start": v(-164.7, -395.88) * mm, "mid": v(-164.56, -403.74) * mm, "end": v(-160.77, -410.63) * mm});
            skArc(sketch, "E268", {"start": v(-167.92, -439.22) * mm, "mid": v(-160.9, -425.78) * mm, "end": v(-160.77, -410.63) * mm});
            skArc(sketch, "E269", {"start": v(-167.92, -439.22) * mm, "mid": v(-177.94, -429.94) * mm, "end": v(-190.53, -424.63) * mm});
            skArc(sketch, "E270", {"start": v(-185.12, -323.09) * mm, "mid": v(-181.91, -353.6) * mm, "end": v(-151.4, -356.8) * mm});
            skArc(sketch, "E271", {"start": v(-151.4, -356.8) * mm, "mid": v(-143.92, -362.9) * mm, "end": v(-134.69, -360.12) * mm});
            skArc(sketch, "E272", {"start": v(-134.69, -360.12) * mm, "mid": v(-128.55, -356.09) * mm, "end": v(-128.93, -348.75) * mm});
            skArc(sketch, "E273", {"start": v(-113.21, -335.4) * mm, "mid": v(-123.58, -339.13) * mm, "end": v(-128.93, -348.75) * mm});
            skArc(sketch, "E274", {"start": v(-113.21, -335.4) * mm, "mid": v(-100.23, -349.57) * mm, "end": v(-87.24, -335.4) * mm});
            skArc(sketch, "E275", {"start": v(-87.24, -335.4) * mm, "mid": v(-96.04, -306.19) * mm, "end": v(-120.5, -287.95) * mm});
            skArc(sketch, "E276", {"start": v(-120.5, -287.95) * mm, "mid": v(-159.76, -292.75) * mm, "end": v(-185.12, -323.09) * mm});
            skArc(sketch, "E277", {"start": v(-204.95, -411.54) * mm, "mid": v(-198.55, -418.98) * mm, "end": v(-190.53, -424.63) * mm});
            skArc(sketch, "E278", {"start": v(-204.95, -411.54) * mm, "mid": v(-211.1, -410.67) * mm, "end": v(-217.1, -412.32) * mm});
            skArc(sketch, "E279", {"start": v(-243.21, -395.7) * mm, "mid": v(-234, -410.59) * mm, "end": v(-216.53, -412.04) * mm});
            skArc(sketch, "E280", {"start": v(-243.21, -395.7) * mm, "mid": v(-247.83, -390.7) * mm, "end": v(-254.23, -393.02) * mm});
            skArc(sketch, "E281", {"start": v(-228.03, -315.86) * mm, "mid": v(-227.45, -312.8) * mm, "end": v(-228.03, -309.72) * mm});
            skArc(sketch, "E282", {"start": v(-228.03, -315.86) * mm, "mid": v(-251.04, -340.16) * mm, "end": v(-273.88, -364.6) * mm});
            skArc(sketch, "E283", {"start": v(-293.67, -361.09) * mm, "mid": v(-284.72, -368.2) * mm, "end": v(-273.88, -364.6) * mm});
            skArc(sketch, "E284", {"start": v(-293.67, -361.09) * mm, "mid": v(-294.44, -357.18) * mm, "end": v(-296.51, -353.77) * mm});
            skArc(sketch, "E285", {"start": v(-296.51, -353.77) * mm, "mid": v(-301.4, -354.29) * mm, "end": v(-305.05, -357.57) * mm});
            skArc(sketch, "E286", {"start": v(-315.36, -350.52) * mm, "mid": v(-312.41, -357.26) * mm, "end": v(-305.05, -357.57) * mm});
            skArc(sketch, "E287", {"start": v(-216.52, -362.97) * mm, "mid": v(-217.54, -356.07) * mm, "end": v(-224.42, -354.91) * mm});
            skLineSegment(sketch, "E288", {"start": v(-224.42, -354.91) * mm, "end": v(-242.32, -381.04) * mm});
            skArc(sketch, "E289", {"start": v(-242.32, -381.04) * mm, "mid": v(-241.56, -389.98) * mm, "end": v(-232.65, -391.03) * mm});
            skArc(sketch, "E290", {"start": v(-232.65, -391.03) * mm, "mid": v(-223.29, -387.5) * mm, "end": v(-218.14, -378.93) * mm});
            skArc(sketch, "E291", {"start": v(-218.14, -378.93) * mm, "mid": v(-216.21, -371.07) * mm, "end": v(-216.52, -362.97) * mm});
            skArc(sketch, "E292", {"start": v(-310.36, -432.54) * mm, "mid": v(-279.38, -416.91) * mm, "end": v(-254.23, -393.02) * mm});
            skArc(sketch, "E293", {"start": v(-369.05, -429.03) * mm, "mid": v(-339.89, -433.83) * mm, "end": v(-310.36, -432.54) * mm});
            skArc(sketch, "E294", {"start": v(-369.05, -429.03) * mm, "mid": v(-380.8, -429.93) * mm, "end": v(-390.58, -436.49) * mm});
            skArc(sketch, "E295", {"start": v(-396.28, -424.22) * mm, "mid": v(-395.04, -431.1) * mm, "end": v(-390.58, -436.49) * mm});
            skArc(sketch, "E296", {"start": v(-396.28, -424.22) * mm, "mid": v(-403.78, -420.86) * mm, "end": v(-408.68, -427.46) * mm});
            skArc(sketch, "E297", {"start": v(-400.6, -397.36) * mm, "mid": v(-415.65, -409.45) * mm, "end": v(-408.68, -427.46) * mm});
            skArc(sketch, "E298", {"start": v(-400.6, -397.36) * mm, "mid": v(-398.55, -391.1) * mm, "end": v(-400.6, -384.82) * mm});
            skArc(sketch, "E299", {"start": v(-400.6, -337.48) * mm, "mid": v(-402.2, -361.15) * mm, "end": v(-400.6, -384.82) * mm});
            skArc(sketch, "E300", {"start": v(-400.6, -337.48) * mm, "mid": v(-404.44, -315.3) * mm, "end": v(-424.57, -305.24) * mm});
            skArc(sketch, "E301", {"start": v(-380.08, -289.26) * mm, "mid": v(-408.21, -280.85) * mm, "end": v(-424.57, -305.24) * mm});
            skArc(sketch, "E302", {"start": v(-380.08, -289.26) * mm, "mid": v(-375.14, -290.06) * mm, "end": v(-372.18, -286.04) * mm});
            skArc(sketch, "E303", {"start": v(-337.3, -266.77) * mm, "mid": v(-357.49, -271.44) * mm, "end": v(-372.18, -286.04) * mm});
            skArc(sketch, "E304", {"start": v(-337.3, -266.77) * mm, "mid": v(-341.45, -282.27) * mm, "end": v(-339.7, -298.22) * mm});
            skArc(sketch, "E305", {"start": v(-339.7, -298.22) * mm, "mid": v(-334.08, -298.9) * mm, "end": v(-328.96, -296.49) * mm});
            skArc(sketch, "E306", {"start": v(-301.07, -305.97) * mm, "mid": v(-313.73, -297.46) * mm, "end": v(-328.96, -296.49) * mm});
            skArc(sketch, "E307", {"start": v(-301.07, -305.97) * mm, "mid": v(-308.05, -313.44) * mm, "end": v(-312.67, -322.56) * mm});
            skArc(sketch, "E308", {"start": v(-321.3, -333.78) * mm, "mid": v(-316.2, -328.78) * mm, "end": v(-312.67, -322.56) * mm});
            skArc(sketch, "E309", {"start": v(-321.3, -333.78) * mm, "mid": v(-321.36, -337.46) * mm, "end": v(-321.3, -341.13) * mm});
            skArc(sketch, "E310", {"start": v(-315.36, -350.52) * mm, "mid": v(-317.46, -345.28) * mm, "end": v(-321.3, -341.13) * mm});
            skArc(sketch, "E311", {"start": v(-347.17, -373.18) * mm, "mid": v(-348.26, -358.12) * mm, "end": v(-363.13, -355.5) * mm});
            skArc(sketch, "E312", {"start": v(-363.13, -355.5) * mm, "mid": v(-369.47, -372.5) * mm, "end": v(-363.13, -389.48) * mm});
            skArc(sketch, "E313", {"start": v(-363.13, -389.48) * mm, "mid": v(-343.06, -403.54) * mm, "end": v(-318.56, -403.61) * mm});
            skArc(sketch, "E314", {"start": v(-347.17, -373.18) * mm, "mid": v(-335.07, -377.4) * mm, "end": v(-323.23, -372.5) * mm});
            skArc(sketch, "E315", {"start": v(-312.17, -378.07) * mm, "mid": v(-316.23, -372.35) * mm, "end": v(-323.23, -372.5) * mm});
            skArc(sketch, "E316", {"start": v(-312.17, -378.07) * mm, "mid": v(-308.07, -384.34) * mm, "end": v(-302.71, -389.58) * mm});
            skArc(sketch, "E317", {"start": v(-306.13, -398.25) * mm, "mid": v(-302.58, -394.64) * mm, "end": v(-302.71, -389.58) * mm});
            skArc(sketch, "E318", {"start": v(-318.56, -403.61) * mm, "mid": v(-311.77, -402.26) * mm, "end": v(-306.13, -398.25) * mm});
            skSolve(sketch);
        }
        {
            var Q0;
            Q0=makeQuery(id+"F2.imprint","IMPRINT",FACE,{"disambiguationData":[TD([[makeQuery(id+"F2.imprint","IMPRINT",EDGE,{"derivedFrom":sQuery(id+"F2.wireOp",EDGE,"E19")}),1.0]])]});
            extrude(context, id + "F3", {"entities" : qUnion([Q0]), "operationType" : NewBodyOperationType.REMOVE, "oppositeDirection" : true, "depth" : 10 * mm, "offsetDistance" : 25 * mm});
        }
        {
            var Q0;
            Q0=makeQuery(id+"F1.opExtrude","SWEPT_EDGE",EDGE,{"disambiguationData":[OSD([sQuery(id+"F0.wireOp",EDGE,"E1"),sQuery(id+"F0.wireOp",EDGE,"E2")])]});
            var Q1;
            Q1=makeQuery(id+"F1.opExtrude","SWEPT_EDGE",EDGE,{"disambiguationData":[OSD([sQuery(id+"F0.wireOp",EDGE,"E2"),sQuery(id+"F0.wireOp",EDGE,"E3")])]});
            var Q2;
            Q2=makeQuery(id+"F1.opExtrude","SWEPT_EDGE",EDGE,{"disambiguationData":[OSD([sQuery(id+"F0.wireOp",EDGE,"E3"),sQuery(id+"F0.wireOp",EDGE,"E4")])]});
            var Q3;
            Q3=makeQuery(id+"F1.opExtrude","SWEPT_EDGE",EDGE,{"disambiguationData":[OSD([sQuery(id+"F0.wireOp",EDGE,"E4"),sQuery(id+"F0.wireOp",EDGE,"E5")])]});
            var Q4;
            Q4=makeQuery(id+"F1.opExtrude","SWEPT_EDGE",EDGE,{"disambiguationData":[OSD([sQuery(id+"F0.wireOp",EDGE,"E0"),sQuery(id+"F0.wireOp",EDGE,"E5")])]});
            var Q5;
            Q5=makeQuery(id+"F1.opExtrude","SWEPT_EDGE",EDGE,{"disambiguationData":[OSD([sQuery(id+"F0.wireOp",EDGE,"E0"),sQuery(id+"F0.wireOp",EDGE,"E1")])]});
            fillet(context, id + "F4", {"entities" : qUnion([Q0, Q1, Q2, Q3, Q4, Q5]), "radius" : 20 * mm, "tangentPropagation" : true, "allowEdgeOverflow" : false});
        }
    });
